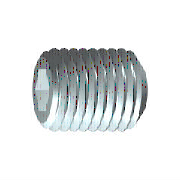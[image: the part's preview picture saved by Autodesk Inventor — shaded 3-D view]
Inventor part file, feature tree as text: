
AUTODESK INVENTOR PART (.ipt)
format: ipt  version: 2019 (Build 230136000, 136)  size: 163,328 bytes
history: native  units: mm (DEFAULTED — no unit token found)
features: other x2, sketch x2, extrude x1, plane x1
ambient origin geometry x8: Origin, YZ Plane, XZ Plane, XY Plane, X Axis, Y Axis, Z Axis, Center Point
bodies: Solid1 (feature_tree)
feature tree (6):
  other  "Körper"
  extrude  "Loch"  TaperAngle=60.0deg  [1 undecoded]
  other  "Work Axis1"
  plane  "Work Plane1"
  sketch  "Skizze1"  dims[d0=3.0mm d1=60.0deg]
  sketch  "Skizze2"  dims[d2=5.0mm d3=2.886751mm d6=90.0deg d4=0.0mm d5=8.0mm d7=0.49076mm d8=45.0deg d21=10.0mm d9=0.0mm d11=8.0mm d12=0.0mm d13=0.49076mm d14=45.0deg d15=0.0mm d29=0.49076mm d30=0.49076mm d31=0.0mm]
note: 1 required parameter value undecoded (feature->parameter linkage not recoverable at this tier; creation-order binding heuristic only, values carry confidence <= 0.55)
